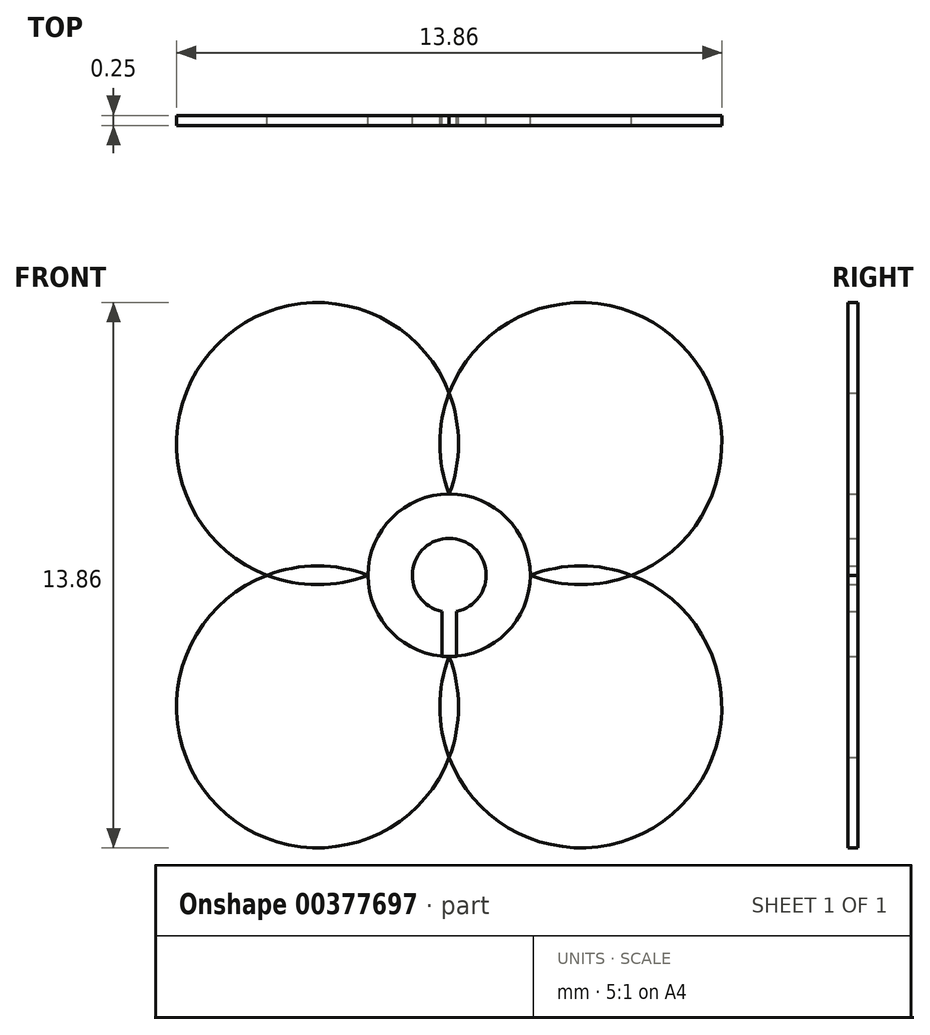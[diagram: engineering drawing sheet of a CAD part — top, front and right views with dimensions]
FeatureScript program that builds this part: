
annotation { "Feature Type Name" : "Feature", "Feature Type Description" : "" }
export const myFeature = defineFeature(function(context is Context, id is Id, definition is map)
    precondition{}
    {
        {
            var Q0;
            Q0=qCreatedBy(makeId("Front.planeOp"),FACE);
            var sketch = newSketch(context, id + "F0", { "sketchPlane" : qUnion([Q0])});
            skCircle(sketch, "E0", {"center": v(0, 0) * mm, "radius": 2.06 * mm});
            skArc(sketch, "E1", {"start": v(0, 2.06) * mm, "mid": v(-5.88, 5.88) * mm, "end": v(-2.06, 0) * mm});
            skArc(sketch, "E2", {"start": v(2.06, 0) * mm, "mid": v(5.88, 5.88) * mm, "end": v(0, 2.06) * mm});
            skArc(sketch, "E3", {"start": v(0, -2.06) * mm, "mid": v(5.88, -5.88) * mm, "end": v(2.06, 0) * mm});
            skArc(sketch, "E4", {"start": v(-2.06, 0) * mm, "mid": v(-5.88, -5.88) * mm, "end": v(0, -2.06) * mm});
            skSolve(sketch);
        }
        {
            var Q0;
            {var subQ0=sQuery(id+"F0.wireOp",EDGE,"E2");var subQ1=sQuery(id+"F0.wireOp",EDGE,"E1");var subQ6=makeQuery(id+"F0.imprint","INTERSECT",VERTEX,{"derivedFrom":[subQ1,subQ0]});Q0=makeQuery(id+"F0.imprint","IMPRINT",FACE,{"disambiguationData":[TD([[makeQuery(id+"F0.imprint","IMPRINT",EDGE,{"disambiguationData":[TD([[subQ6,1.0]])],"derivedFrom":subQ0}),1.0]])]});}
            var Q1;
            {var subQ0=sQuery(id+"F0.wireOp",EDGE,"E3");var subQ1=sQuery(id+"F0.wireOp",EDGE,"E2");var subQ6=makeQuery(id+"F0.imprint","INTERSECT",VERTEX,{"derivedFrom":[subQ1,subQ0]});Q1=makeQuery(id+"F0.imprint","IMPRINT",FACE,{"disambiguationData":[TD([[makeQuery(id+"F0.imprint","IMPRINT",EDGE,{"disambiguationData":[TD([[subQ6,1.0]])],"derivedFrom":subQ0}),1.0]])]});}
            var Q2;
            {var subQ0=sQuery(id+"F0.wireOp",EDGE,"E2");var subQ1=sQuery(id+"F0.wireOp",EDGE,"E1");var subQ6=makeQuery(id+"F0.imprint","INTERSECT",VERTEX,{"derivedFrom":[subQ1,subQ0]});Q2=makeQuery(id+"F0.imprint","IMPRINT",FACE,{"disambiguationData":[TD([[makeQuery(id+"F0.imprint","IMPRINT",EDGE,{"disambiguationData":[TD([[subQ6,-1.0]])],"derivedFrom":subQ1}),1.0]])]});}
            var Q3;
            {var subQ0=sQuery(id+"F0.wireOp",EDGE,"E4");var subQ1=sQuery(id+"F0.wireOp",EDGE,"E1");var subQ6=makeQuery(id+"F0.imprint","INTERSECT",VERTEX,{"derivedFrom":[subQ1,subQ0]});Q3=makeQuery(id+"F0.imprint","IMPRINT",FACE,{"disambiguationData":[TD([[makeQuery(id+"F0.imprint","IMPRINT",EDGE,{"disambiguationData":[TD([[subQ6,-1.0]])],"derivedFrom":subQ0}),1.0]])]});}
            extrude(context, id + "F1", {"entities" : qUnion([Q0, Q1, Q2, Q3]), "depth" : 0.25 * mm});
        }
        {
            var Q0;
            Q0=qCreatedBy(makeId("Front.planeOp"),FACE);
            var sketch = newSketch(context, id + "F2", { "sketchPlane" : qUnion([Q0])});
            skArc(sketch, "E5", {"start": v(0.19, -0.92) * mm, "mid": v(0, 0.94) * mm, "end": v(-0.19, -0.92) * mm});
            skLineSegment(sketch, "E6.bottom", {"start": v(0, -0.94) * mm, "end": v(0, -0.94) * mm});
            skLineSegment(sketch, "E6.top", {"start": v(0, -2.07) * mm, "end": v(0, -2.07) * mm});
            skLineSegment(sketch, "E7.top", {"start": v(-0.19, -2.06) * mm, "end": v(0.19, -2.06) * mm});
            skLineSegment(sketch, "E7.left", {"start": v(-0.19, -0.92) * mm, "end": v(-0.19, -2.06) * mm});
            skLineSegment(sketch, "E7.right", {"start": v(0.19, -0.92) * mm, "end": v(0.19, -2.06) * mm});
            skSolve(sketch);
        }
        {
            var Q0;
            Q0 = qSketchRegion(id + "F2", true);
            extrude(context, id + "F3", {"entities" : qUnion([Q0]), "depth" : 0.25 * mm});
        }
    });
